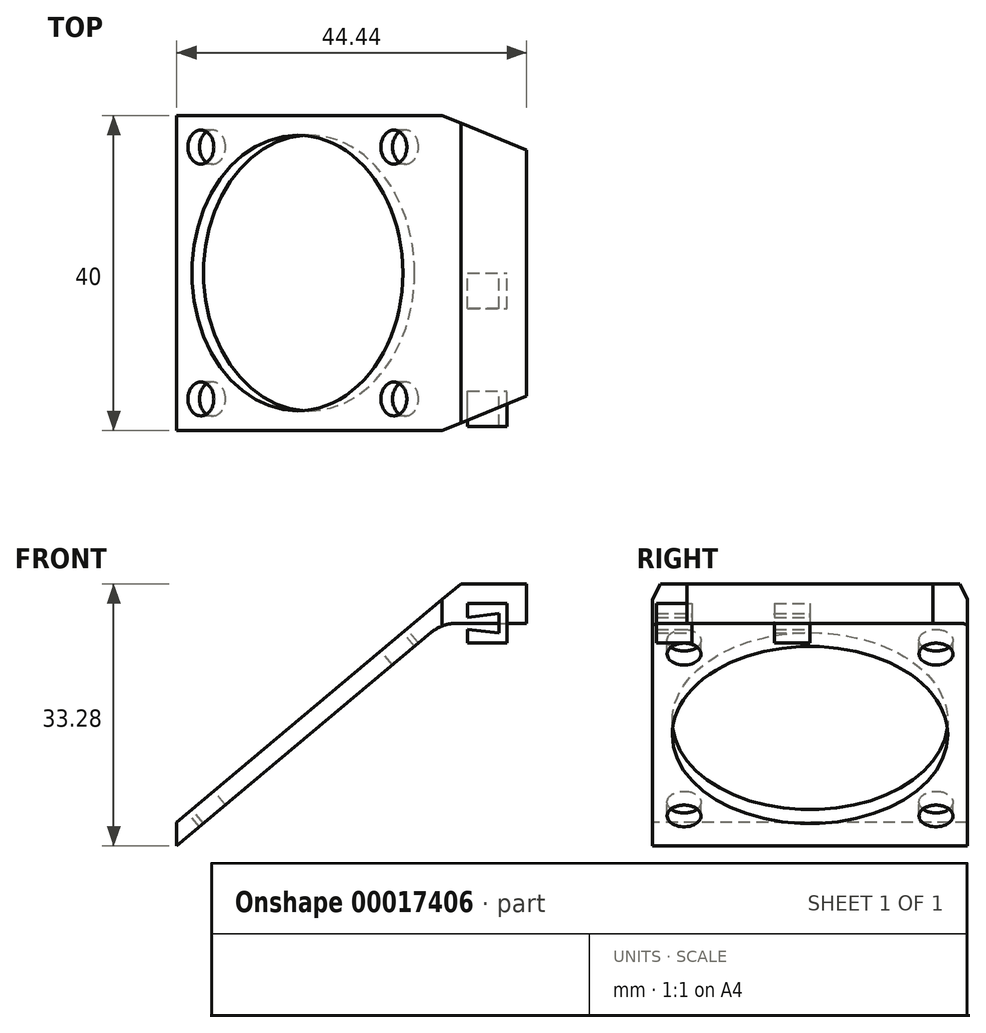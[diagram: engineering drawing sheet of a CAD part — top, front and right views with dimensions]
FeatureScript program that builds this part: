
annotation { "Feature Type Name" : "Feature", "Feature Type Description" : "" }
export const myFeature = defineFeature(function(context is Context, id is Id, definition is map)
    precondition{}
    {
        {
            var Q0;
            Q0=qCreatedBy(makeId("Front.planeOp"),FACE);
            var sketch = newSketch(context, id + "F0", { "sketchPlane" : qUnion([Q0])});
            skLineSegment(sketch, "E0.rect.bottom", {"start": v(-2.5, 2.5) * mm, "end": v(2.5, 2.5) * mm});
            skLineSegment(sketch, "E0.rect.top", {"start": v(-2.5, -2.5) * mm, "end": v(2.5, -2.5) * mm});
            skLineSegment(sketch, "E0.rect.left", {"start": v(-2.5, 2.5) * mm, "end": v(-2.5, -2.5) * mm});
            skLineSegment(sketch, "E0.rect.right", {"start": v(2.5, 2.5) * mm, "end": v(2.5, -2.5) * mm});
            skPoint(sketch, "E0.rect.middle", {"position": v(0, 0) * mm});
            skSolve(sketch);
        }
        {
            var Q0;
            Q0=makeQuery(id+"F0.imprint","IMPRINT",FACE,{"disambiguationData":[TD([[makeQuery(id+"F0.imprint","IMPRINT",EDGE,{"derivedFrom":sQuery(id+"F0.wireOp",EDGE,"E0.rect.bottom")}),-1.0]])]});
            extrude(context, id + "F1", {"entities" : qUnion([Q0]), "depth" : 4.5 * mm});
        }
        {
            var Q0;
            Q0=makeQuery(id+"F1.opExtrude","CAP_FACE",FACE,{"disambiguationData":[OSD([sQuery(id+"F0.wireOp",EDGE,"E0.rect.bottom"),sQuery(id+"F0.wireOp",EDGE,"E0.rect.top"),sQuery(id+"F0.wireOp",EDGE,"E0.rect.left"),sQuery(id+"F0.wireOp",EDGE,"E0.rect.right")])],"isStart":true});
            var sketch = newSketch(context, id + "F2", { "sketchPlane" : qUnion([Q0])});
            skLineSegment(sketch, "E1", {"start": v(2.5, 0.75) * mm, "end": v(-1.47, 1.25) * mm});
            skLineSegment(sketch, "E2", {"start": v(-1.47, 1.25) * mm, "end": v(-1.47, -1.25) * mm});
            skLineSegment(sketch, "E3", {"start": v(-1.47, -1.25) * mm, "end": v(2.5, -0.75) * mm});
            skLineSegment(sketch, "E4", {"start": v(2.5, -0.75) * mm, "end": v(2.5, 0.75) * mm});
            skSolve(sketch);
        }
        {
            var Q0;
            Q0=makeQuery(id+"F2.imprint","IMPRINT",FACE,{"disambiguationData":[TD([[makeQuery(id+"F2.imprint","IMPRINT",EDGE,{"derivedFrom":sQuery(id+"F2.wireOp",EDGE,"E1")}),1.0]])]});
            extrude(context, id + "F3", {"entities" : qUnion([Q0]), "operationType" : NewBodyOperationType.REMOVE, "oppositeDirection" : true, "depth" : 25 * mm});
        }
        {
            var Q0;
            Q0=qCreatedBy(makeId("Top.planeOp"),FACE);
            var sketch = newSketch(context, id + "F4", { "sketchPlane" : qUnion([Q0])});
            skLineSegment(sketch, "E5.rect.bottom", {"start": v(-5.74, 20) * mm, "end": v(5, 15.6) * mm});
            skLineSegment(sketch, "E5.rect.top", {"start": v(-5.74, -20) * mm, "end": v(5, -15.61) * mm});
            skLineSegment(sketch, "E5.rect.left", {"start": v(-5.74, 20) * mm, "end": v(-5.74, -20) * mm});
            skLineSegment(sketch, "E5.rect.right", {"start": v(5, 15.6) * mm, "end": v(5, -15.61) * mm});
            skPoint(sketch, "E5.rect.middle", {"position": v(0, 0) * mm});
            skSolve(sketch);
        }
        {
            var Q0;
            Q0=makeQuery(id+"F4.imprint","IMPRINT",FACE,{"disambiguationData":[TD([[makeQuery(id+"F4.imprint","IMPRINT",EDGE,{"derivedFrom":sQuery(id+"F4.wireOp",EDGE,"E5.rect.bottom")}),-1.0]])]});
            extrude(context, id + "F5", {"entities" : qUnion([Q0]), "depth" : 5 * mm});
        }
        {
            var Q0;
            Q0=qCreatedBy(makeId("Front.planeOp"),FACE);
            var sketch = newSketch(context, id + "F6", { "sketchPlane" : qUnion([Q0])});
            skLineSegment(sketch, "E6", {"start": v(-5.74, 0) * mm, "end": v(-39.44, -28.28) * mm});
            skLineSegment(sketch, "E7", {"start": v(-39.44, -28.28) * mm, "end": v(-39.44, -25.28) * mm});
            skLineSegment(sketch, "E8", {"start": v(-5.74, 3) * mm, "end": v(-5.74, 0) * mm});
            skLineSegment(sketch, "E9", {"start": v(-5.74, 3) * mm, "end": v(-39.44, -25.28) * mm});
            skSolve(sketch);
        }
        {
            var Q0;
            Q0=makeQuery(id+"F6.imprint","IMPRINT",FACE,{"disambiguationData":[TD([[makeQuery(id+"F6.imprint","IMPRINT",EDGE,{"derivedFrom":sQuery(id+"F6.wireOp",EDGE,"E6")}),-1.0]])]});
            var Q1;
            Q1=makeQuery(id+"F5.opExtrude","SWEPT_FACE",FACE,{"disambiguationData":[OSD([sQuery(id+"F4.wireOp",EDGE,"E5.rect.bottom")])]});
            extrude(context, id + "F7", {"entities" : qUnion([Q0]), "operationType" : NewBodyOperationType.ADD, "endBound" : BoundingType.SYMMETRIC, "oppositeDirection" : true, "endBoundEntityFace" : qUnion([Q1]), "depth" : 40 * mm});
        }
        {
            var Q0;
            Q0=makeQuery(id+"F7.opExtrude","SWEPT_FACE",FACE,{"disambiguationData":[OSD([sQuery(id+"F6.wireOp",EDGE,"E9")])]});
            var sketch = newSketch(context, id + "F8", { "sketchPlane" : qUnion([Q0])});
            skLineSegment(sketch, "E10.bottom", {"start": v(-46.47, 20) * mm, "end": v(-6.47, 20) * mm, "construction": true});
            skLineSegment(sketch, "E10.top", {"start": v(-46.47, -20) * mm, "end": v(-6.47, -20) * mm, "construction": true});
            skLineSegment(sketch, "E10.left", {"start": v(-46.47, 20) * mm, "end": v(-46.47, -20) * mm, "construction": true});
            skLineSegment(sketch, "E10.right", {"start": v(-6.47, 20) * mm, "end": v(-6.47, -20) * mm, "construction": true});
            skLineSegment(sketch, "E11.bottom", {"start": v(-42.47, 16) * mm, "end": v(-10.47, 16) * mm, "construction": true});
            skLineSegment(sketch, "E11.top", {"start": v(-42.47, -16) * mm, "end": v(-10.47, -16) * mm, "construction": true});
            skLineSegment(sketch, "E11.left", {"start": v(-42.47, 16) * mm, "end": v(-42.47, -16) * mm, "construction": true});
            skLineSegment(sketch, "E11.right", {"start": v(-10.47, 16) * mm, "end": v(-10.47, -16) * mm, "construction": true});
            skLineSegment(sketch, "E12", {"start": v(-46.47, 0) * mm, "end": v(-6.47, 0) * mm, "construction": true});
            skLineSegment(sketch, "E13", {"start": v(-26.47, 20) * mm, "end": v(-26.47, -20) * mm, "construction": true});
            skCircle(sketch, "E14", {"center": v(-42.47, 16) * mm, "radius": 2.15 * mm});
            skCircle(sketch, "E15", {"center": v(-10.47, 16) * mm, "radius": 2.15 * mm});
            skCircle(sketch, "E16", {"center": v(-10.47, -16) * mm, "radius": 2.15 * mm});
            skCircle(sketch, "E17", {"center": v(-42.47, -16) * mm, "radius": 2.15 * mm});
            skCircle(sketch, "E18", {"center": v(-26.47, 0) * mm, "radius": 17.5 * mm});
            skSolve(sketch);
        }
        {
            var Q0;
            Q0=makeQuery(id+"F8.imprint","IMPRINT",FACE,{"disambiguationData":[TD([[makeQuery(id+"F8.imprint","IMPRINT",EDGE,{"derivedFrom":sQuery(id+"F8.wireOp",EDGE,"E14")}),1.0]])]});
            var Q1;
            Q1=makeQuery(id+"F8.imprint","IMPRINT",FACE,{"disambiguationData":[TD([[makeQuery(id+"F8.imprint","IMPRINT",EDGE,{"derivedFrom":sQuery(id+"F8.wireOp",EDGE,"E15")}),1.0]])]});
            var Q2;
            Q2=makeQuery(id+"F8.imprint","IMPRINT",FACE,{"disambiguationData":[TD([[makeQuery(id+"F8.imprint","IMPRINT",EDGE,{"derivedFrom":sQuery(id+"F8.wireOp",EDGE,"E16")}),1.0]])]});
            var Q3;
            Q3=makeQuery(id+"F8.imprint","IMPRINT",FACE,{"disambiguationData":[TD([[makeQuery(id+"F8.imprint","IMPRINT",EDGE,{"derivedFrom":sQuery(id+"F8.wireOp",EDGE,"E17")}),1.0]])]});
            var Q4;
            Q4=makeQuery(id+"F8.imprint","IMPRINT",FACE,{"disambiguationData":[TD([[makeQuery(id+"F8.imprint","IMPRINT",EDGE,{"derivedFrom":sQuery(id+"F8.wireOp",EDGE,"E18")}),1.0]])]});
            extrude(context, id + "F9", {"entities" : qUnion([Q0, Q1, Q2, Q3, Q4]), "operationType" : NewBodyOperationType.REMOVE, "oppositeDirection" : true, "depth" : 25 * mm});
        }
        {
            var Q0;
            Q0=makeQuery(id+"F1.opExtrude","SWEPT_BODY",BODY,{"disambiguationData":[OSD([sQuery(id+"F0.wireOp",EDGE,"E0.rect.bottom"),sQuery(id+"F0.wireOp",EDGE,"E0.rect.top"),sQuery(id+"F0.wireOp",EDGE,"E0.rect.left"),sQuery(id+"F0.wireOp",EDGE,"E0.rect.right")])]});
            transform(context, id + "F10", {"entities" : qUnion([Q0]), "transformType" : TransformType.TRANSLATION_3D, "dx" : 0 * mm, "dy" : -15 * mm, "dz" : 0 * mm, "makeCopy" : true});
        }
        {
            var Q0;
            Q0=qCreatedBy(makeId("Front.planeOp"),FACE);
            var sketch = newSketch(context, id + "F11", { "sketchPlane" : qUnion([Q0])});
            skLineSegment(sketch, "E19", {"start": v(-5.74, 3) * mm, "end": v(-3.35, 5) * mm});
            skLineSegment(sketch, "E20", {"start": v(-3.35, 5) * mm, "end": v(-5.74, 5) * mm});
            skLineSegment(sketch, "E21", {"start": v(-5.74, 5) * mm, "end": v(-5.74, 3) * mm});
            skSolve(sketch);
        }
        {
            var Q0;
            Q0 = qSketchRegion(id + "F11", true);
            extrude(context, id + "F12", {"entities" : qUnion([Q0]), "operationType" : NewBodyOperationType.REMOVE, "endBound" : BoundingType.SYMMETRIC, "oppositeDirection" : true, "depth" : 40 * mm});
        }
        {
            var Q0;
            Q0=makeQuery(id+"F7.boolean.opBoolean","MERGE",EDGE,{"derivedFrom":[makeQuery(id+"F5.opExtrude","CAP_EDGE",EDGE,{"disambiguationData":[OSD([sQuery(id+"F4.wireOp",EDGE,"E5.rect.left")])],"isStart":true}),makeQuery(id+"F7.opExtrude","SWEPT_EDGE",EDGE,{"disambiguationData":[OSD([sQuery(id+"F6.wireOp",EDGE,"E6"),sQuery(id+"F6.wireOp",EDGE,"E8")])]})]});
            var Q1;
            Q1=makeQuery(id+"F12.boolean.opBoolean","COPY",EDGE,{"derivedFrom":makeQuery(id+"F12.opExtrude","SWEPT_EDGE",EDGE,{"disambiguationData":[OSD([sQuery(id+"F11.wireOp",EDGE,"E19"),sQuery(id+"F11.wireOp",EDGE,"E20")])]})});
            fillet(context, id + "F13", {"entities" : qUnion([Q0, Q1]), "radius" : 5 * mm, "tangentPropagation" : true, "allowEdgeOverflow" : false});
        }
    });
